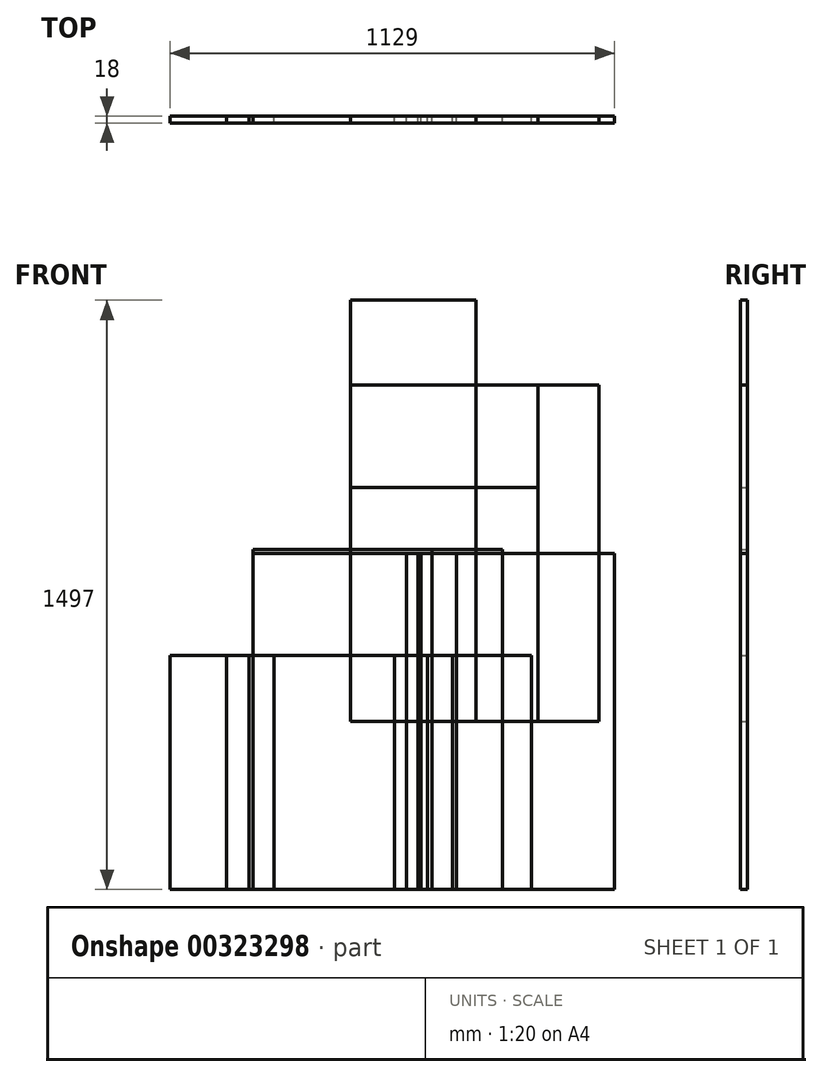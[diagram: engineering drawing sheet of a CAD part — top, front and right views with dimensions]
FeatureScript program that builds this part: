
annotation { "Feature Type Name" : "Feature", "Feature Type Description" : "" }
export const myFeature = defineFeature(function(context is Context, id is Id, definition is map)
    precondition{}
    {
        {
            var Q0;
            Q0=qCreatedBy(makeId("Front.planeOp"),FACE);
            var sketch = newSketch(context, id + "F0", { "sketchPlane" : qUnion([Q0])});
            skLineSegment(sketch, "E0.bottom", {"start": v(0, 0) * mm, "end": v(476, 0) * mm});
            skLineSegment(sketch, "E0.top", {"start": v(0, 854) * mm, "end": v(476, 854) * mm});
            skLineSegment(sketch, "E0.left", {"start": v(0, 0) * mm, "end": v(0, 854) * mm});
            skLineSegment(sketch, "E0.right", {"start": v(476, 0) * mm, "end": v(476, 854) * mm});
            skSolve(sketch);
        }
        {
            var Q0;
            Q0 = qSketchRegion(id + "F0", true);
            extrude(context, id + "F1", {"entities" : qUnion([Q0]), "depth" : 18 * mm, "offsetDistance" : 25 * mm});
        }
        {
            var Q0;
            Q0=qCreatedBy(makeId("Front.planeOp"),FACE);
            var sketch = newSketch(context, id + "F2", { "sketchPlane" : qUnion([Q0])});
            skLineSegment(sketch, "E1.bottom", {"start": v(0, 0) * mm, "end": v(476, 0) * mm});
            skLineSegment(sketch, "E1.top", {"start": v(0, 594) * mm, "end": v(476, 594) * mm});
            skLineSegment(sketch, "E1.left", {"start": v(0, 0) * mm, "end": v(0, 594) * mm});
            skLineSegment(sketch, "E1.right", {"start": v(476, 0) * mm, "end": v(476, 594) * mm});
            skSolve(sketch);
        }
        {
            var Q0;
            Q0 = qSketchRegion(id + "F2", true);
            extrude(context, id + "F3", {"entities" : qUnion([Q0]), "depth" : 18 * mm, "offsetDistance" : 25 * mm});
        }
        {
            var Q0;
            Q0=qCreatedBy(makeId("Front.planeOp"),FACE);
            var sketch = newSketch(context, id + "F4", { "sketchPlane" : qUnion([Q0])});
            skLineSegment(sketch, "E2.bottom", {"start": v(0, 0) * mm, "end": v(630, 0) * mm});
            skLineSegment(sketch, "E2.top", {"start": v(0, 854) * mm, "end": v(630, 854) * mm});
            skLineSegment(sketch, "E2.left", {"start": v(0, 0) * mm, "end": v(0, 854) * mm});
            skLineSegment(sketch, "E2.right", {"start": v(630, 0) * mm, "end": v(630, 854) * mm});
            skSolve(sketch);
        }
        {
            var Q0;
            Q0 = qSketchRegion(id + "F4", true);
            extrude(context, id + "F5", {"entities" : qUnion([Q0]), "depth" : 18 * mm, "offsetDistance" : 25 * mm});
        }
        {
            var Q0;
            Q0=qCreatedBy(makeId("Front.planeOp"),FACE);
            var sketch = newSketch(context, id + "F6", { "sketchPlane" : qUnion([Q0])});
            skLineSegment(sketch, "E3.bottom", {"start": v(-248, -427) * mm, "end": v(178, -427) * mm});
            skLineSegment(sketch, "E3.top", {"start": v(-248, 427) * mm, "end": v(178, 427) * mm});
            skLineSegment(sketch, "E3.left", {"start": v(-248, -427) * mm, "end": v(-248, 427) * mm});
            skLineSegment(sketch, "E3.right", {"start": v(178, -427) * mm, "end": v(178, 427) * mm});
            skSolve(sketch);
        }
        {
            var Q0;
            Q0 = qSketchRegion(id + "F6", true);
            extrude(context, id + "F7", {"entities" : qUnion([Q0]), "depth" : 18 * mm, "offsetDistance" : 25 * mm});
        }
        {
            var Q0;
            Q0=qCreatedBy(makeId("Front.planeOp"),FACE);
            var sketch = newSketch(context, id + "F8", { "sketchPlane" : qUnion([Q0])});
            skLineSegment(sketch, "E4.bottom", {"start": v(-248, -427) * mm, "end": v(268, -427) * mm});
            skLineSegment(sketch, "E4.top", {"start": v(-248, 427) * mm, "end": v(268, 427) * mm});
            skLineSegment(sketch, "E4.left", {"start": v(-248, -427) * mm, "end": v(-248, 427) * mm});
            skLineSegment(sketch, "E4.right", {"start": v(268, -427) * mm, "end": v(268, 427) * mm});
            skSolve(sketch);
        }
        {
            var Q0;
            Q0 = qSketchRegion(id + "F8", true);
            extrude(context, id + "F9", {"entities" : qUnion([Q0]), "depth" : 18 * mm, "offsetDistance" : 25 * mm});
        }
        {
            var Q0;
            Q0=qCreatedBy(makeId("Front.planeOp"),FACE);
            var sketch = newSketch(context, id + "F10", { "sketchPlane" : qUnion([Q0])});
            skLineSegment(sketch, "E5.bottom", {"start": v(-248, -427) * mm, "end": v(141, -427) * mm});
            skLineSegment(sketch, "E5.top", {"start": v(-248, 427) * mm, "end": v(141, 427) * mm});
            skLineSegment(sketch, "E5.left", {"start": v(-248, -427) * mm, "end": v(-248, 427) * mm});
            skLineSegment(sketch, "E5.right", {"start": v(141, -427) * mm, "end": v(141, 427) * mm});
            skSolve(sketch);
        }
        {
            var Q0;
            Q0 = qSketchRegion(id + "F10", true);
            extrude(context, id + "F11", {"entities" : qUnion([Q0]), "depth" : 18 * mm, "offsetDistance" : 25 * mm});
        }
        {
            var Q0;
            Q0=qCreatedBy(makeId("Front.planeOp"),FACE);
            var sketch = newSketch(context, id + "F12", { "sketchPlane" : qUnion([Q0])});
            skLineSegment(sketch, "E6.bottom", {"start": v(-248, -427) * mm, "end": v(207, -427) * mm});
            skLineSegment(sketch, "E6.top", {"start": v(-248, 437) * mm, "end": v(207, 437) * mm});
            skLineSegment(sketch, "E6.left", {"start": v(-248, -427) * mm, "end": v(-248, 437) * mm});
            skLineSegment(sketch, "E6.right", {"start": v(207, -427) * mm, "end": v(207, 437) * mm});
            skSolve(sketch);
        }
        {
            var Q0;
            Q0 = qSketchRegion(id + "F12", true);
            extrude(context, id + "F13", {"entities" : qUnion([Q0]), "depth" : 18 * mm, "offsetDistance" : 25 * mm});
        }
        {
            var Q0;
            Q0=qCreatedBy(makeId("Front.planeOp"),FACE);
            var sketch = newSketch(context, id + "F14", { "sketchPlane" : qUnion([Q0])});
            skLineSegment(sketch, "E7.bottom", {"start": v(-248, -427) * mm, "end": v(670, -427) * mm});
            skLineSegment(sketch, "E7.top", {"start": v(-248, 427) * mm, "end": v(670, 427) * mm});
            skLineSegment(sketch, "E7.left", {"start": v(-248, -427) * mm, "end": v(-248, 427) * mm});
            skLineSegment(sketch, "E7.right", {"start": v(670, -427) * mm, "end": v(670, 427) * mm});
            skSolve(sketch);
        }
        {
            var Q0;
            Q0 = qSketchRegion(id + "F14", true);
            extrude(context, id + "F15", {"entities" : qUnion([Q0]), "depth" : 18 * mm, "offsetDistance" : 25 * mm});
        }
        {
            var Q0;
            Q0=qCreatedBy(makeId("Front.planeOp"),FACE);
            var sketch = newSketch(context, id + "F16", { "sketchPlane" : qUnion([Q0])});
            skLineSegment(sketch, "E8.bottom", {"start": v(0, 0) * mm, "end": v(318, 0) * mm});
            skLineSegment(sketch, "E8.top", {"start": v(0, 1070) * mm, "end": v(318, 1070) * mm});
            skLineSegment(sketch, "E8.left", {"start": v(0, 0) * mm, "end": v(0, 1070) * mm});
            skLineSegment(sketch, "E8.right", {"start": v(318, 0) * mm, "end": v(318, 1070) * mm});
            skSolve(sketch);
        }
        {
            var Q0;
            Q0 = qSketchRegion(id + "F16", true);
            extrude(context, id + "F17", {"entities" : qUnion([Q0]), "depth" : 18 * mm, "offsetDistance" : 25 * mm});
        }
        {
            var Q0;
            Q0=qCreatedBy(makeId("Front.planeOp"),FACE);
            var sketch = newSketch(context, id + "F18", { "sketchPlane" : qUnion([Q0])});
            skLineSegment(sketch, "E9.bottom", {"start": v(-248, -427) * mm, "end": v(171, -427) * mm});
            skLineSegment(sketch, "E9.top", {"start": v(-248, 427) * mm, "end": v(171, 427) * mm});
            skLineSegment(sketch, "E9.left", {"start": v(-248, -427) * mm, "end": v(-248, 427) * mm});
            skLineSegment(sketch, "E9.right", {"start": v(171, -427) * mm, "end": v(171, 427) * mm});
            skSolve(sketch);
        }
        {
            var Q0;
            Q0 = qSketchRegion(id + "F18", true);
            extrude(context, id + "F19", {"entities" : qUnion([Q0]), "depth" : 18 * mm, "offsetDistance" : 25 * mm});
        }
        {
            var Q0;
            Q0=qCreatedBy(makeId("Front.planeOp"),FACE);
            var sketch = newSketch(context, id + "F20", { "sketchPlane" : qUnion([Q0])});
            skLineSegment(sketch, "E10.bottom", {"start": v(-315, -427) * mm, "end": v(111, -427) * mm});
            skLineSegment(sketch, "E10.top", {"start": v(-315, 167) * mm, "end": v(111, 167) * mm});
            skLineSegment(sketch, "E10.left", {"start": v(-315, -427) * mm, "end": v(-315, 167) * mm});
            skLineSegment(sketch, "E10.right", {"start": v(111, -427) * mm, "end": v(111, 167) * mm});
            skSolve(sketch);
        }
        {
            var Q0;
            Q0 = qSketchRegion(id + "F20", true);
            extrude(context, id + "F21", {"entities" : qUnion([Q0]), "depth" : 18 * mm, "offsetDistance" : 25 * mm});
        }
        {
            var Q0;
            Q0=qCreatedBy(makeId("Front.planeOp"),FACE);
            var sketch = newSketch(context, id + "F22", { "sketchPlane" : qUnion([Q0])});
            skLineSegment(sketch, "E11.bottom", {"start": v(-258, -427) * mm, "end": v(258, -427) * mm});
            skLineSegment(sketch, "E11.top", {"start": v(-258, 167) * mm, "end": v(258, 167) * mm});
            skLineSegment(sketch, "E11.left", {"start": v(-258, -427) * mm, "end": v(-258, 167) * mm});
            skLineSegment(sketch, "E11.right", {"start": v(258, -427) * mm, "end": v(258, 167) * mm});
            skSolve(sketch);
        }
        {
            var Q0;
            Q0 = qSketchRegion(id + "F22", true);
            extrude(context, id + "F23", {"entities" : qUnion([Q0]), "depth" : 18 * mm, "offsetDistance" : 25 * mm});
        }
        {
            var Q0;
            Q0=qCreatedBy(makeId("Front.planeOp"),FACE);
            var sketch = newSketch(context, id + "F24", { "sketchPlane" : qUnion([Q0])});
            skLineSegment(sketch, "E12.bottom", {"start": v(-194.5, -427) * mm, "end": v(194.5, -427) * mm});
            skLineSegment(sketch, "E12.top", {"start": v(-194.5, 167) * mm, "end": v(194.5, 167) * mm});
            skLineSegment(sketch, "E12.left", {"start": v(-194.5, -427) * mm, "end": v(-194.5, 167) * mm});
            skLineSegment(sketch, "E12.right", {"start": v(194.5, -427) * mm, "end": v(194.5, 167) * mm});
            skSolve(sketch);
        }
        {
            var Q0;
            Q0 = qSketchRegion(id + "F24", true);
            extrude(context, id + "F25", {"entities" : qUnion([Q0]), "depth" : 18 * mm, "offsetDistance" : 25 * mm});
        }
        {
            var Q0;
            Q0=qCreatedBy(makeId("Front.planeOp"),FACE);
            var sketch = newSketch(context, id + "F26", { "sketchPlane" : qUnion([Q0])});
            skLineSegment(sketch, "E13.bottom", {"start": v(-248, -427) * mm, "end": v(386, -427) * mm});
            skLineSegment(sketch, "E13.top", {"start": v(-248, 437) * mm, "end": v(386, 437) * mm});
            skLineSegment(sketch, "E13.left", {"start": v(-248, -427) * mm, "end": v(-248, 437) * mm});
            skLineSegment(sketch, "E13.right", {"start": v(386, -427) * mm, "end": v(386, 437) * mm});
            skSolve(sketch);
        }
        {
            var Q0;
            Q0 = qSketchRegion(id + "F26", true);
            extrude(context, id + "F27", {"entities" : qUnion([Q0]), "depth" : 18 * mm, "offsetDistance" : 25 * mm});
        }
        {
            var Q0;
            Q0=qCreatedBy(makeId("Front.planeOp"),FACE);
            var sketch = newSketch(context, id + "F28", { "sketchPlane" : qUnion([Q0])});
            skLineSegment(sketch, "E14.bottom", {"start": v(-459, -427) * mm, "end": v(459, -427) * mm});
            skLineSegment(sketch, "E14.top", {"start": v(-459, 167) * mm, "end": v(459, 167) * mm});
            skLineSegment(sketch, "E14.left", {"start": v(-459, -427) * mm, "end": v(-459, 167) * mm});
            skLineSegment(sketch, "E14.right", {"start": v(459, -427) * mm, "end": v(459, 167) * mm});
            skSolve(sketch);
        }
        {
            var Q0;
            Q0 = qSketchRegion(id + "F28", true);
            extrude(context, id + "F29", {"entities" : qUnion([Q0]), "depth" : 18 * mm, "offsetDistance" : 25 * mm});
        }
    });
